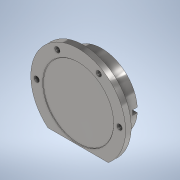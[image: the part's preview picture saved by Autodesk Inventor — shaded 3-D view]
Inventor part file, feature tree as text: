
AUTODESK INVENTOR PART (.ipt)
format: ipt  version: 2020 (Build 240168000, 168)  size: 180,736 bytes
history: native  units: mm
features: extrude x5, sketch x5, other x3, reference x2, plane x1, fillet x1, projected_geometry x1
ambient origin geometry x8: Origin, YZ Plane, XZ Plane, XY Plane, X Axis, Y Axis, Z Axis, Center Point
bodies: 实体1 (feature_tree)
feature tree (18):
  plane  "工作平面1"
  extrude  "拉伸1"  Depth=175.0mm
  extrude  "拉伸2"  Depth=11.0mm TaperAngle=360.0deg
  extrude  "拉伸3"  Depth=10.0mm
  fillet  "圆角1"  Radius=10.0mm
  extrude  "拉伸4"  Depth=38.0mm
  extrude  "拉伸5"  Depth=1.0mm
  sketch  "草图1"  dims[d0=2.0mm d1=175.0mm]
  reference  "参考1"
  reference  "参考2"
  sketch  "草图2"  dims[d2=11.0mm d3=60.0mm d5=360.0deg]
  sketch  "草图3"  dims[d7=12.0mm d8=0.0mm d9=150.0mm d10=10.0mm]
  sketch  "草图4"  dims[d11=38.0mm d12=0.0mm d13=150.0mm]
  sketch  "草图5"  dims[d14=1.0mm d15=0.0mm d16=1.0mm d17=10.0mm d18=200.0mm d19=10.0mm d20=0.0mm d21=3.0mm d22=0.0mm]
  projected_geometry  "投影回路1"
  other  "<userpath>\Desktop\ME_course_project\课设试试\shaft_try_1.iam"
  other  "shaft_try_1.iam"
  other  "xia(1):1"
